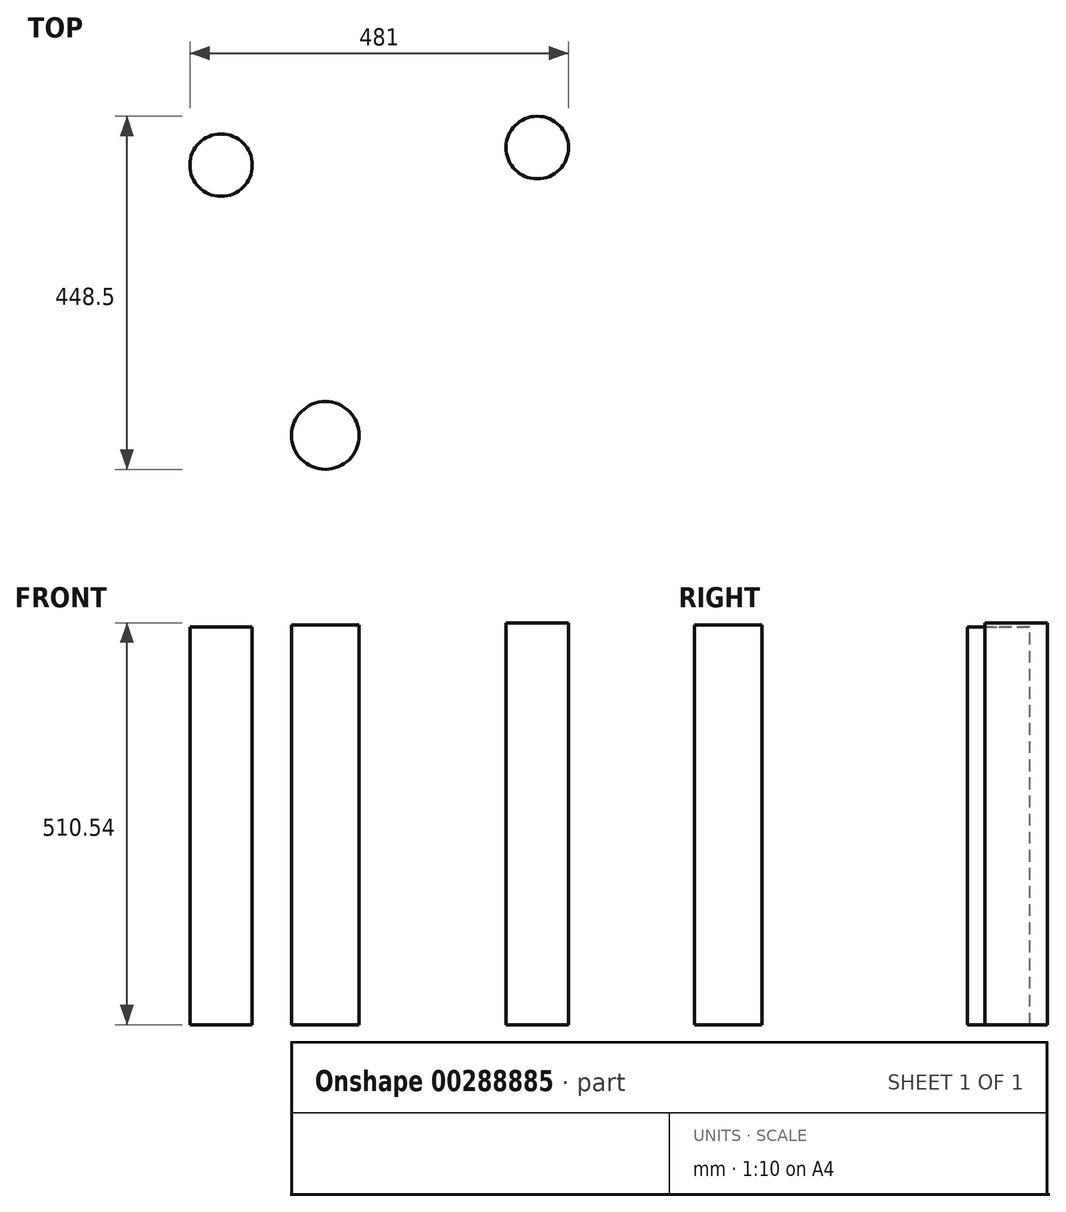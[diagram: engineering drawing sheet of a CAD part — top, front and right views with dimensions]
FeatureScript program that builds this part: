
annotation { "Feature Type Name" : "Feature", "Feature Type Description" : "" }
export const myFeature = defineFeature(function(context is Context, id is Id, definition is map)
    precondition{}
    {
        {
            var Q0;
            Q0=qCreatedBy(makeId("Top.planeOp"),FACE);
            var sketch = newSketch(context, id + "F0", { "sketchPlane" : qUnion([Q0])});
            skLineSegment(sketch, "E0", {"start": v(-47.58, -154.51) * mm, "end": v(188.53, 144.51) * mm});
            skLineSegment(sketch, "E1", {"start": v(188.53, 144.51) * mm, "end": v(-141.65, 148.73) * mm});
            skLineSegment(sketch, "E2", {"start": v(-141.65, 148.73) * mm, "end": v(-47.58, -154.51) * mm});
            skCircle(sketch, "E3", {"center": v(220.42, 168.25) * mm, "radius": 39.76 * mm});
            skCircle(sketch, "E4", {"center": v(-181.18, 145.88) * mm, "radius": 39.64 * mm});
            skCircle(sketch, "E5", {"center": v(-48.7, -197.5) * mm, "radius": 43 * mm});
            skPoint(sketch, "E6", {"position": v(-94.61, -2.89) * mm});
            skLineSegment(sketch, "E7", {"start": v(-111.54, 0) * mm, "end": v(-150.4, 120.9) * mm});
            skCircle(sketch, "E8", {"center": v(-121.53, -13.53) * mm, "radius": 28.95 * mm});
            skText(sketch, "E9", { "text": "18.5 d", "fontName": "OpenSans-Regular.ttf"});
            skText(sketch, "E10", { "text": "15.2\" d", "fontName": "OpenSans-Regular.ttf"});
            skText(sketch, "E11", { "text": "13.4\" d", "fontName": "OpenSans-Regular.ttf"});
            skText(sketch, "E12", { "text": "11.4\" d", "fontName": "OpenSans-Regular.ttf"});
            skLineSegment(sketch, "E13", {"start": v(70.47, -5) * mm, "end": v(220.67, -354.94) * mm});
            skText(sketch, "E14", { "text": "15 y to parking", "fontName": "OpenSans-Regular.ttf"});
            const initialGuessF0  = {"E9": [-0.02483, -0.26174, 1, 0, 0.02847], "E10": [0.2473, 0.19754, 1, 0, 0.02095], "E11": [-0.264, 0.17728, 1, 0, 0.02382], "E12": [-0.22777, 0.0036, 1, 0, 0.01846], "E14": [0.14557, -0.17997, 1, 0, 0.02218]};
            skSetInitialGuess(sketch, initialGuessF0);
            skSolve(sketch);
        }
        {
            var Q0;
            Q0=sQuery(id+"F0.wireOp",EDGE,"E4");
            extrude(context, id + "F1", {"bodyType" : ToolBodyType.SURFACE, "surfaceEntities" : qUnion([Q0]), "depth" : 251.46 * mm, "hasSecondDirection" : true, "secondDirectionOppositeDirection" : true, "secondDirectionDepth" : 254 * mm});
        }
        {
            var Q0;
            Q0=sQuery(id+"F0.wireOp",EDGE,"E3");
            extrude(context, id + "F2", {"bodyType" : ToolBodyType.SURFACE, "surfaceEntities" : qUnion([Q0]), "depth" : 256.54 * mm, "hasSecondDirection" : true, "secondDirectionOppositeDirection" : true, "secondDirectionDepth" : 254 * mm});
        }
        {
            var Q0;
            Q0=sQuery(id+"F0.wireOp",EDGE,"E5");
            extrude(context, id + "F3", {"bodyType" : ToolBodyType.SURFACE, "surfaceEntities" : qUnion([Q0]), "depth" : 254 * mm, "hasSecondDirection" : true, "secondDirectionOppositeDirection" : true, "secondDirectionDepth" : 254 * mm});
        }
    });
